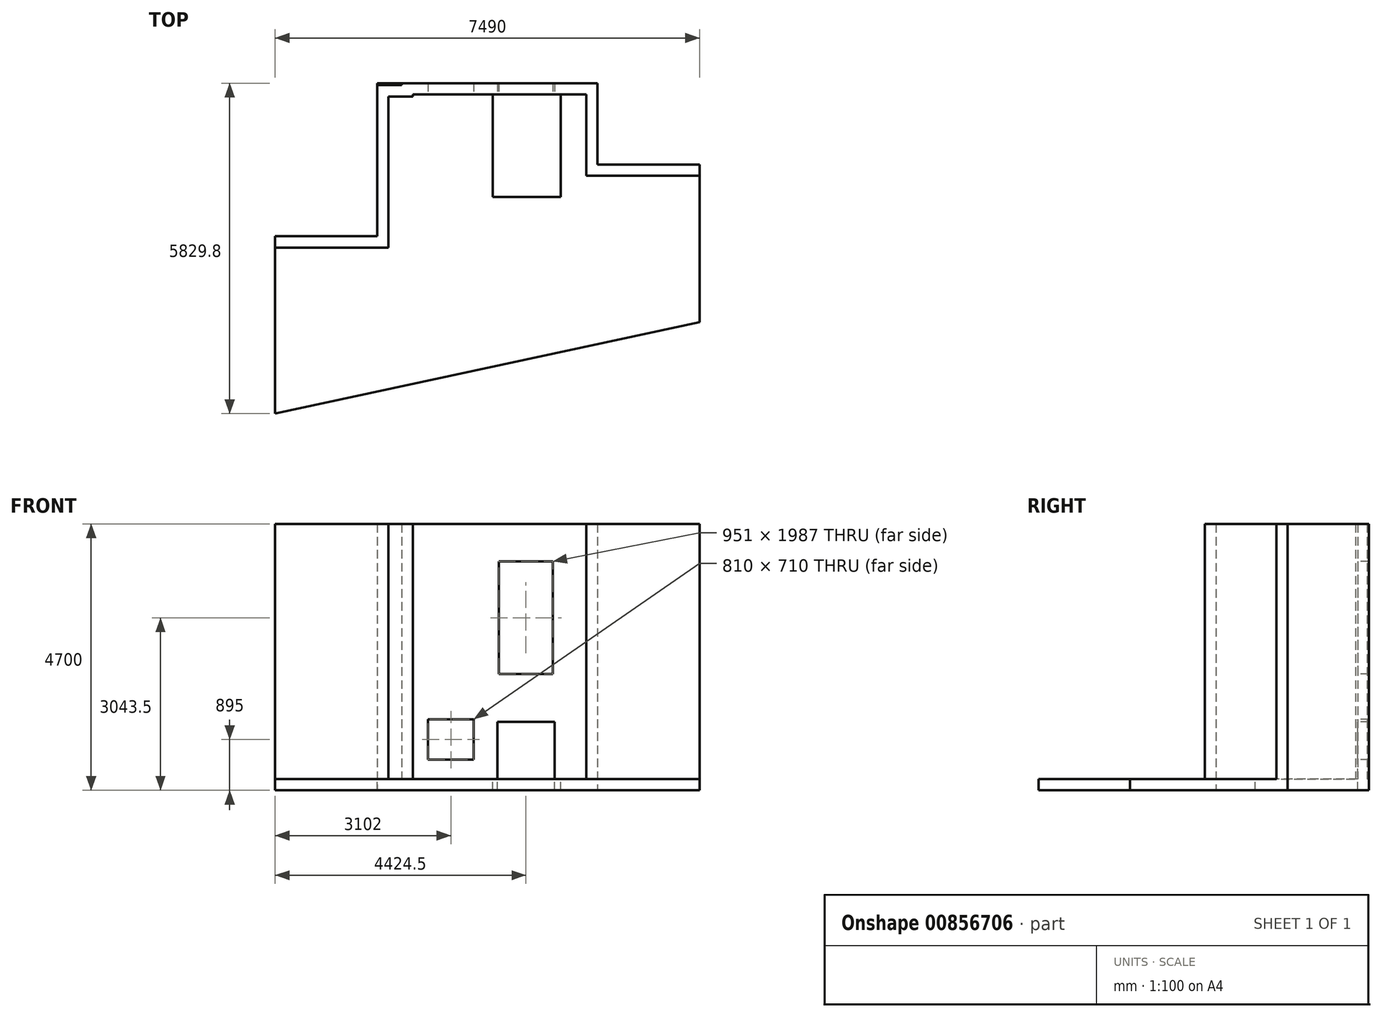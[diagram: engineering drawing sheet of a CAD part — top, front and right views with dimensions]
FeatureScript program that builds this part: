
annotation { "Feature Type Name" : "Feature", "Feature Type Description" : "" }
export const myFeature = defineFeature(function(context is Context, id is Id, definition is map)
    precondition{}
    {
        {
            var Q0;
            Q0=qCreatedBy(makeId("Top.planeOp"),FACE);
            var sketch = newSketch(context, id + "F0", { "sketchPlane" : qUnion([Q0])});
            skLineSegment(sketch, "E0", {"start": v(-2000, -2700) * mm, "end": v(0, -2700) * mm});
            skLineSegment(sketch, "E1", {"start": v(0, -2700) * mm, "end": v(0, -35) * mm});
            skLineSegment(sketch, "E2", {"start": v(432, 0) * mm, "end": v(3490, 0) * mm});
            skLineSegment(sketch, "E3", {"start": v(3490, 0) * mm, "end": v(3490, -1435) * mm});
            skLineSegment(sketch, "E4", {"start": v(3490, -1435) * mm, "end": v(5490, -1435) * mm});
            skLineSegment(sketch, "E5.top", {"start": v(0, -35) * mm, "end": v(432, -35) * mm});
            skLineSegment(sketch, "E5.right", {"start": v(432, 0) * mm, "end": v(432, -35) * mm});
            skPoint(sketch, "E6", {"position": v(0, 0) * mm});
            skLineSegment(sketch, "E7.0", {"start": v(3690, -1235) * mm, "end": v(5490, -1235) * mm});
            skLineSegment(sketch, "E7.1", {"start": v(3690, 200) * mm, "end": v(3690, -1235) * mm});
            skLineSegment(sketch, "E7.2", {"start": v(232, 200) * mm, "end": v(3690, 200) * mm});
            skLineSegment(sketch, "E7.3", {"start": v(-2000, -2500) * mm, "end": v(-200, -2500) * mm});
            skLineSegment(sketch, "E7.4", {"start": v(-200, -2500) * mm, "end": v(-200, 165) * mm});
            skLineSegment(sketch, "E7.5", {"start": v(-200, 165) * mm, "end": v(232, 165) * mm});
            skLineSegment(sketch, "E7.6", {"start": v(232, 200) * mm, "end": v(232, 165) * mm});
            skLineSegment(sketch, "E8", {"start": v(5490, -1235) * mm, "end": v(5490, -1435) * mm});
            skLineSegment(sketch, "E9", {"start": v(-2000, -2500) * mm, "end": v(-2000, -2700) * mm});
            skSolve(sketch);
        }
        {
            var Q0;
            Q0 = qSketchRegion(id + "F0", true);
            extrude(context, id + "F1", {"entities" : qUnion([Q0]), "depth" : 4500 * mm, "offsetDistance" : 25 * mm});
        }
        {
            var Q0;
            Q0=qCreatedBy(makeId("Top.planeOp"),FACE);
            var sketch = newSketch(context, id + "F2", { "sketchPlane" : qUnion([Q0])});
            skLineSegment(sketch, "E10.bottom", {"start": v(-2000, -5629.8) * mm, "end": v(5490, -4020.2) * mm});
            skLineSegment(sketch, "E10.left", {"start": v(-2000, -5629.8) * mm, "end": v(-2000, -2500) * mm});
            skLineSegment(sketch, "E10.right", {"start": v(5490, -4020.2) * mm, "end": v(5490, -1235) * mm});
            skLineSegment(sketch, "E11", {"start": v(3690, 200) * mm, "end": v(-200, 200) * mm});
            skLineSegment(sketch, "E12", {"start": v(5490, -1235) * mm, "end": v(3690, -1235) * mm});
            skLineSegment(sketch, "E13", {"start": v(3690, -1235) * mm, "end": v(3690, 200) * mm});
            skLineSegment(sketch, "E14", {"start": v(-2000, -2500) * mm, "end": v(-200, -2500) * mm});
            skLineSegment(sketch, "E15", {"start": v(-200, -2500) * mm, "end": v(-200, 200) * mm});
            skLineSegment(sketch, "E16", {"start": v(3490, -1435) * mm, "end": v(3490, -4450) * mm, "construction": true});
            skLineSegment(sketch, "E17", {"start": v(0, -2700) * mm, "end": v(0, -5200) * mm, "construction": true});
            skSolve(sketch);
        }
        {
            var Q0;
            Q0 = qSketchRegion(id + "F2", true);
            extrude(context, id + "F3", {"entities" : qUnion([Q0]), "operationType" : NewBodyOperationType.ADD, "oppositeDirection" : true, "depth" : 200 * mm, "offsetDistance" : 25 * mm});
        }
        {
            var Q0;
            Q0=makeQuery(id+"F1.opExtrude","SWEPT_FACE",FACE,{"disambiguationData":[OSD([sQuery(id+"F0.wireOp",EDGE,"E2")])]});
            var sketch = newSketch(context, id + "F4", { "sketchPlane" : qUnion([Q0])});
            skLineSegment(sketch, "E18.bottom", {"start": v(1949, 3837) * mm, "end": v(2900, 3837) * mm});
            skLineSegment(sketch, "E18.top", {"start": v(1949, 1850) * mm, "end": v(2900, 1850) * mm});
            skLineSegment(sketch, "E18.left", {"start": v(1949, 3837) * mm, "end": v(1949, 1850) * mm});
            skLineSegment(sketch, "E18.right", {"start": v(2900, 3837) * mm, "end": v(2900, 1850) * mm});
            skLineSegment(sketch, "E19.bottom", {"start": v(2930, -200) * mm, "end": v(1920, -200) * mm});
            skLineSegment(sketch, "E19.top", {"start": v(2930, 1010) * mm, "end": v(1920, 1010) * mm});
            skLineSegment(sketch, "E19.left", {"start": v(2930, -200) * mm, "end": v(2930, 1010) * mm});
            skLineSegment(sketch, "E19.right", {"start": v(1920, -200) * mm, "end": v(1920, 1010) * mm});
            skLineSegment(sketch, "E20.bottom", {"start": v(1507, 340) * mm, "end": v(697, 340) * mm});
            skLineSegment(sketch, "E20.top", {"start": v(1507, 1050) * mm, "end": v(697, 1050) * mm});
            skLineSegment(sketch, "E20.left", {"start": v(1507, 340) * mm, "end": v(1507, 1050) * mm});
            skLineSegment(sketch, "E20.right", {"start": v(697, 340) * mm, "end": v(697, 1050) * mm});
            skSolve(sketch);
        }
        {
            var Q0;
            Q0 = qSketchRegion(id + "F4", true);
            extrude(context, id + "F5", {"entities" : qUnion([Q0]), "operationType" : NewBodyOperationType.REMOVE, "endBound" : BoundingType.UP_TO_NEXT, "oppositeDirection" : true, "depth" : 25 * mm, "offsetDistance" : 25 * mm});
        }
        {
            var Q0;
            {var subQ0=sQuery(id+"F2.wireOp",EDGE,"E10.bottom");var subQ1=sQuery(id+"F2.wireOp",EDGE,"E10.right");var subQ2=sQuery(id+"F2.wireOp",EDGE,"E10.left");Q0=makeQuery(id+"F3.boolean.opBoolean","SPLIT",FACE,{"disambiguationData":[TD([makeQuery(id+"F1.opExtrude","SWEPT_FACE",FACE,{"disambiguationData":[OSD([sQuery(id+"F0.wireOp",EDGE,"E0")])]})])],"derivedFrom":makeQuery(id+"F3.opExtrude","CAP_FACE",FACE,{"disambiguationData":[OSD([subQ0,subQ2,subQ1,sQuery(id+"F2.wireOp",EDGE,"E11"),sQuery(id+"F2.wireOp",EDGE,"E12"),sQuery(id+"F2.wireOp",EDGE,"E13"),sQuery(id+"F2.wireOp",EDGE,"E14"),sQuery(id+"F2.wireOp",EDGE,"E15")])],"isStart":true})});}
            var sketch = newSketch(context, id + "F6", { "sketchPlane" : qUnion([Q0])});
            skLineSegment(sketch, "E21.bottom", {"start": v(1840, 0) * mm, "end": v(3040, 0) * mm});
            skLineSegment(sketch, "E21.top", {"start": v(1840, -1810) * mm, "end": v(3040, -1810) * mm});
            skLineSegment(sketch, "E21.left", {"start": v(1840, 0) * mm, "end": v(1840, -1810) * mm});
            skLineSegment(sketch, "E21.right", {"start": v(3040, 0) * mm, "end": v(3040, -1810) * mm});
            skSolve(sketch);
        }
        {
            var Q0;
            Q0 = qSketchRegion(id + "F6", true);
            extrude(context, id + "F7", {"entities" : qUnion([Q0]), "operationType" : NewBodyOperationType.REMOVE, "endBound" : BoundingType.UP_TO_NEXT, "oppositeDirection" : true, "depth" : 25 * mm, "offsetDistance" : 25 * mm});
        }
    });
